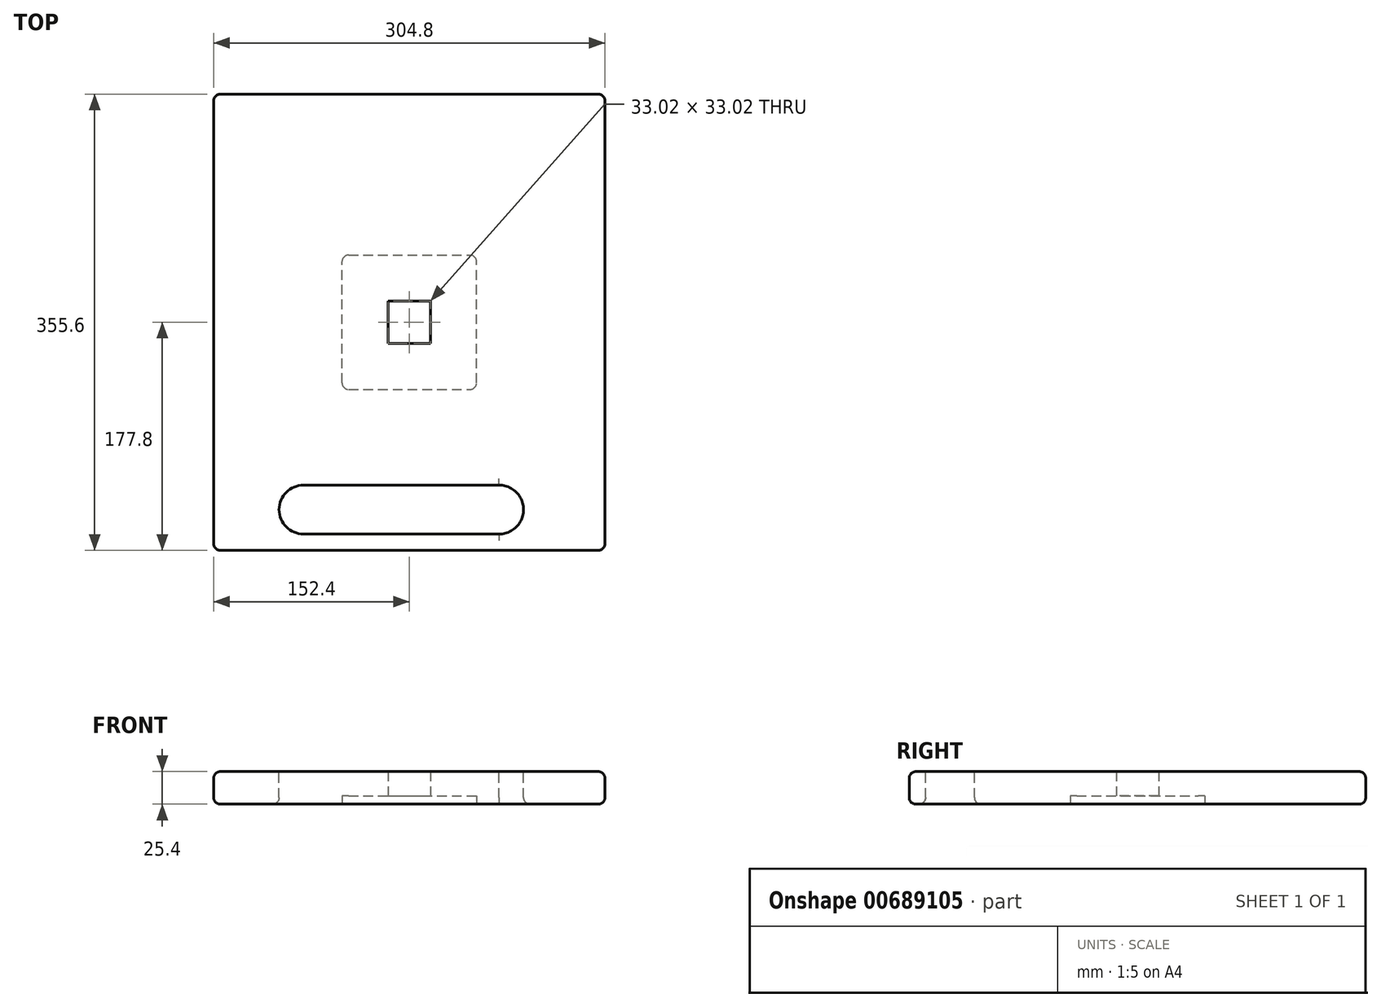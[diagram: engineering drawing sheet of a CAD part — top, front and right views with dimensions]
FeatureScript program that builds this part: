
annotation { "Feature Type Name" : "Feature", "Feature Type Description" : "" }
export const myFeature = defineFeature(function(context is Context, id is Id, definition is map)
    precondition{}
    {
        {
            var Q0;
            Q0=qCreatedBy(makeId("Top.planeOp"),FACE);
            var sketch = newSketch(context, id + "F0", { "sketchPlane" : qUnion([Q0])});
            skLineSegment(sketch, "E0.bottom", {"start": v(-16.51, 16.51) * mm, "end": v(16.51, 16.51) * mm});
            skLineSegment(sketch, "E0.top", {"start": v(-16.51, -16.51) * mm, "end": v(16.51, -16.51) * mm});
            skLineSegment(sketch, "E0.left", {"start": v(-16.51, 16.51) * mm, "end": v(-16.51, -16.51) * mm});
            skLineSegment(sketch, "E0.right", {"start": v(16.51, 16.51) * mm, "end": v(16.51, -16.51) * mm});
            skLineSegment(sketch, "E1.bottom", {"start": v(-152.4, 177.8) * mm, "end": v(152.4, 177.8) * mm});
            skLineSegment(sketch, "E1.top", {"start": v(-152.4, -177.8) * mm, "end": v(152.4, -177.8) * mm});
            skLineSegment(sketch, "E1.left", {"start": v(-152.4, 177.8) * mm, "end": v(-152.4, -177.8) * mm});
            skLineSegment(sketch, "E1.right", {"start": v(152.4, 177.8) * mm, "end": v(152.4, -177.8) * mm});
            skSolve(sketch);
        }
        {
            var Q0;
            Q0=makeQuery(id+"F0.imprint","IMPRINT",FACE,{"disambiguationData":[TD([[makeQuery(id+"F0.imprint","IMPRINT",EDGE,{"derivedFrom":sQuery(id+"F0.wireOp",EDGE,"E0.bottom")}),1.0]])]});
            extrude(context, id + "F1", {"entities" : qUnion([Q0]), "depth" : 25.4 * mm, "offsetDistance" : 25.4 * mm});
        }
        {
            var Q0;
            Q0=makeQuery(id+"F1.opExtrude","CAP_FACE",FACE,{"disambiguationData":[OSD([sQuery(id+"F0.wireOp",EDGE,"E0.bottom"),sQuery(id+"F0.wireOp",EDGE,"E0.top"),sQuery(id+"F0.wireOp",EDGE,"E0.left"),sQuery(id+"F0.wireOp",EDGE,"E0.right"),sQuery(id+"F0.wireOp",EDGE,"E1.bottom"),sQuery(id+"F0.wireOp",EDGE,"E1.top"),sQuery(id+"F0.wireOp",EDGE,"E1.left"),sQuery(id+"F0.wireOp",EDGE,"E1.right")])],"isStart":false});
            var sketch = newSketch(context, id + "F2", { "sketchPlane" : qUnion([Q0])});
            skLineSegment(sketch, "E2", {"start": v(-82.43, -146.05) * mm, "end": v(69.97, -146.05) * mm, "construction": true});
            skLineSegment(sketch, "E3", {"start": v(-82.66, -127) * mm, "end": v(69.74, -127) * mm});
            skArc(sketch, "E4", {"start": v(-82.43, -127) * mm, "mid": v(-101.48, -146.05) * mm, "end": v(-82.43, -165.1) * mm});
            skLineSegment(sketch, "E5", {"start": v(-82.43, -165.1) * mm, "end": v(69.97, -165.1) * mm});
            skArc(sketch, "E6", {"start": v(69.74, -165.1) * mm, "mid": v(89.02, -146.05) * mm, "end": v(69.74, -127) * mm});
            skSolve(sketch);
        }
        {
            var Q0;
            {var subQ2=sQuery(id+"F2.wireOp",EDGE,"E4");Q0=makeQuery(id+"F2.imprint","IMPRINT",FACE,{"disambiguationData":[TD([[makeQuery(id+"F2.imprint","IMPRINT",EDGE,{"derivedFrom":subQ2}),1.0]])]});}
            extrude(context, id + "F3", {"entities" : qUnion([Q0]), "operationType" : NewBodyOperationType.REMOVE, "endBound" : BoundingType.THROUGH_ALL, "oppositeDirection" : true, "depth" : 25.4 * mm, "offsetDistance" : 25.4 * mm});
        }
        {
            var Q0;
            Q0=makeQuery(id+"F1.opExtrude","CAP_EDGE",EDGE,{"disambiguationData":[OSD([sQuery(id+"F0.wireOp",EDGE,"E1.top")])],"isStart":false});
            var Q1;
            Q1=makeQuery(id+"F1.opExtrude","CAP_EDGE",EDGE,{"disambiguationData":[OSD([sQuery(id+"F0.wireOp",EDGE,"E1.top")])],"isStart":true});
            var Q2;
            Q2=makeQuery(id+"F1.opExtrude","CAP_EDGE",EDGE,{"disambiguationData":[OSD([sQuery(id+"F0.wireOp",EDGE,"E1.right")])],"isStart":false});
            var Q3;
            Q3=makeQuery(id+"F1.opExtrude","CAP_EDGE",EDGE,{"disambiguationData":[OSD([sQuery(id+"F0.wireOp",EDGE,"E1.right")])],"isStart":true});
            var Q4;
            Q4=makeQuery(id+"F1.opExtrude","CAP_EDGE",EDGE,{"disambiguationData":[OSD([sQuery(id+"F0.wireOp",EDGE,"E1.left")])],"isStart":false});
            var Q5;
            Q5=makeQuery(id+"F1.opExtrude","CAP_EDGE",EDGE,{"disambiguationData":[OSD([sQuery(id+"F0.wireOp",EDGE,"E1.left")])],"isStart":true});
            var Q6;
            Q6=makeQuery(id+"F1.opExtrude","CAP_EDGE",EDGE,{"disambiguationData":[OSD([sQuery(id+"F0.wireOp",EDGE,"E1.bottom")])],"isStart":true});
            var Q7;
            Q7=makeQuery(id+"F3.boolean.opBoolean","COPY",EDGE,{"derivedFrom":makeQuery(id+"F3.opExtrude","CAP_EDGE",EDGE,{"disambiguationData":[OSD([sQuery(id+"F2.wireOp",EDGE,"E3")])],"isStart":true})});
            var Q8;
            Q8=makeQuery(id+"F3.boolean.opBoolean","COPY",EDGE,{"derivedFrom":makeQuery(id+"F3.opExtrude","CAP_EDGE",EDGE,{"disambiguationData":[OSD([sQuery(id+"F2.wireOp",EDGE,"E4")])],"isStart":true})});
            var Q9;
            Q9=makeQuery(id+"F3.boolean.opBoolean","COPY",EDGE,{"derivedFrom":makeQuery(id+"F3.opExtrude","CAP_EDGE",EDGE,{"disambiguationData":[OSD([sQuery(id+"F2.wireOp",EDGE,"E6")])],"isStart":true})});
            var Q10;
            Q10=makeQuery(id+"F3.boolean.opBoolean","INTERSECT",EDGE,{"derivedFrom":[makeQuery(id+"F1.opExtrude","CAP_FACE",FACE,{"disambiguationData":[OSD([sQuery(id+"F0.wireOp",EDGE,"E0.bottom"),sQuery(id+"F0.wireOp",EDGE,"E0.top"),sQuery(id+"F0.wireOp",EDGE,"E0.left"),sQuery(id+"F0.wireOp",EDGE,"E0.right"),sQuery(id+"F0.wireOp",EDGE,"E1.bottom"),sQuery(id+"F0.wireOp",EDGE,"E1.top"),sQuery(id+"F0.wireOp",EDGE,"E1.left"),sQuery(id+"F0.wireOp",EDGE,"E1.right")])],"isStart":true}),makeQuery(id+"F3.opExtrude","SWEPT_FACE",FACE,{"disambiguationData":[OSD([sQuery(id+"F2.wireOp",EDGE,"E5")])]})]});
            var Q11;
            Q11=makeQuery(id+"F3.boolean.opBoolean","INTERSECT",EDGE,{"derivedFrom":[makeQuery(id+"F1.opExtrude","CAP_FACE",FACE,{"disambiguationData":[OSD([sQuery(id+"F0.wireOp",EDGE,"E0.bottom"),sQuery(id+"F0.wireOp",EDGE,"E0.top"),sQuery(id+"F0.wireOp",EDGE,"E0.left"),sQuery(id+"F0.wireOp",EDGE,"E0.right"),sQuery(id+"F0.wireOp",EDGE,"E1.bottom"),sQuery(id+"F0.wireOp",EDGE,"E1.top"),sQuery(id+"F0.wireOp",EDGE,"E1.left"),sQuery(id+"F0.wireOp",EDGE,"E1.right")])],"isStart":true}),makeQuery(id+"F3.opExtrude","SWEPT_FACE",FACE,{"disambiguationData":[OSD([sQuery(id+"F2.wireOp",EDGE,"E6")])]})]});
            var Q12;
            Q12=makeQuery(id+"F1.opExtrude","CAP_EDGE",EDGE,{"disambiguationData":[OSD([sQuery(id+"F0.wireOp",EDGE,"E1.bottom")])],"isStart":false});
            var Q13;
            Q13=makeQuery(id+"F1.opExtrude","SWEPT_EDGE",EDGE,{"disambiguationData":[OSD([sQuery(id+"F0.wireOp",EDGE,"E1.bottom"),sQuery(id+"F0.wireOp",EDGE,"E1.right")])]});
            var Q14;
            Q14=makeQuery(id+"F1.opExtrude","SWEPT_EDGE",EDGE,{"disambiguationData":[OSD([sQuery(id+"F0.wireOp",EDGE,"E1.bottom"),sQuery(id+"F0.wireOp",EDGE,"E1.left")])]});
            var Q15;
            Q15=makeQuery(id+"F1.opExtrude","SWEPT_EDGE",EDGE,{"disambiguationData":[OSD([sQuery(id+"F0.wireOp",EDGE,"E1.top"),sQuery(id+"F0.wireOp",EDGE,"E1.left")])]});
            var Q16;
            Q16=makeQuery(id+"F1.opExtrude","SWEPT_EDGE",EDGE,{"disambiguationData":[OSD([sQuery(id+"F0.wireOp",EDGE,"E1.top"),sQuery(id+"F0.wireOp",EDGE,"E1.right")])]});
            fillet(context, id + "F4", {"entities" : qUnion([Q0, Q1, Q2, Q3, Q4, Q5, Q6, Q7, Q8, Q9, Q10, Q11, Q12, Q13, Q14, Q15, Q16]), "radius" : 5.08 * mm, "tangentPropagation" : true, "allowEdgeOverflow" : false});
        }
        {
            var Q0;
            Q0=makeQuery(id+"F1.opExtrude","CAP_FACE",FACE,{"disambiguationData":[OSD([sQuery(id+"F0.wireOp",EDGE,"E0.bottom"),sQuery(id+"F0.wireOp",EDGE,"E0.top"),sQuery(id+"F0.wireOp",EDGE,"E0.left"),sQuery(id+"F0.wireOp",EDGE,"E0.right"),sQuery(id+"F0.wireOp",EDGE,"E1.bottom"),sQuery(id+"F0.wireOp",EDGE,"E1.top"),sQuery(id+"F0.wireOp",EDGE,"E1.left"),sQuery(id+"F0.wireOp",EDGE,"E1.right")])],"isStart":true});
            var sketch = newSketch(context, id + "F5", { "sketchPlane" : qUnion([Q0])});
            skLineSegment(sketch, "E7.bottom", {"start": v(-52.39, 52.39) * mm, "end": v(52.39, 52.39) * mm});
            skLineSegment(sketch, "E7.top", {"start": v(-52.39, -52.39) * mm, "end": v(52.39, -52.39) * mm});
            skLineSegment(sketch, "E7.left", {"start": v(-52.39, 52.39) * mm, "end": v(-52.39, -52.39) * mm});
            skLineSegment(sketch, "E7.right", {"start": v(52.39, 52.39) * mm, "end": v(52.39, -52.39) * mm});
            skSolve(sketch);
        }
        {
            var Q0;
            Q0=makeQuery(id+"F5.imprint","IMPRINT",FACE,{"disambiguationData":[TD([[makeQuery(id+"F5.imprint","IMPRINT",EDGE,{"derivedFrom":sQuery(id+"F5.wireOp",EDGE,"E7.bottom")}),-1.0]])]});
            extrude(context, id + "F6", {"entities" : qUnion([Q0]), "operationType" : NewBodyOperationType.REMOVE, "oppositeDirection" : true, "depth" : 6.35 * mm, "offsetDistance" : 25.4 * mm});
        }
        {
            var Q0;
            Q0=makeQuery(id+"F6.boolean.opBoolean","COPY",EDGE,{"derivedFrom":makeQuery(id+"F6.opExtrude","SWEPT_EDGE",EDGE,{"disambiguationData":[OSD([sQuery(id+"F5.wireOp",EDGE,"E7.bottom"),sQuery(id+"F5.wireOp",EDGE,"E7.left")])]})});
            var Q1;
            Q1=makeQuery(id+"F6.boolean.opBoolean","COPY",EDGE,{"derivedFrom":makeQuery(id+"F6.opExtrude","SWEPT_EDGE",EDGE,{"disambiguationData":[OSD([sQuery(id+"F5.wireOp",EDGE,"E7.bottom"),sQuery(id+"F5.wireOp",EDGE,"E7.right")])]})});
            var Q2;
            Q2=makeQuery(id+"F6.boolean.opBoolean","COPY",EDGE,{"derivedFrom":makeQuery(id+"F6.opExtrude","SWEPT_EDGE",EDGE,{"disambiguationData":[OSD([sQuery(id+"F5.wireOp",EDGE,"E7.top"),sQuery(id+"F5.wireOp",EDGE,"E7.left")])]})});
            var Q3;
            Q3=makeQuery(id+"F6.boolean.opBoolean","COPY",EDGE,{"derivedFrom":makeQuery(id+"F6.opExtrude","SWEPT_EDGE",EDGE,{"disambiguationData":[OSD([sQuery(id+"F5.wireOp",EDGE,"E7.top"),sQuery(id+"F5.wireOp",EDGE,"E7.right")])]})});
            fillet(context, id + "F7", {"entities" : qUnion([Q0, Q1, Q2, Q3]), "radius" : 5.08 * mm, "tangentPropagation" : true, "allowEdgeOverflow" : false});
        }
    });
